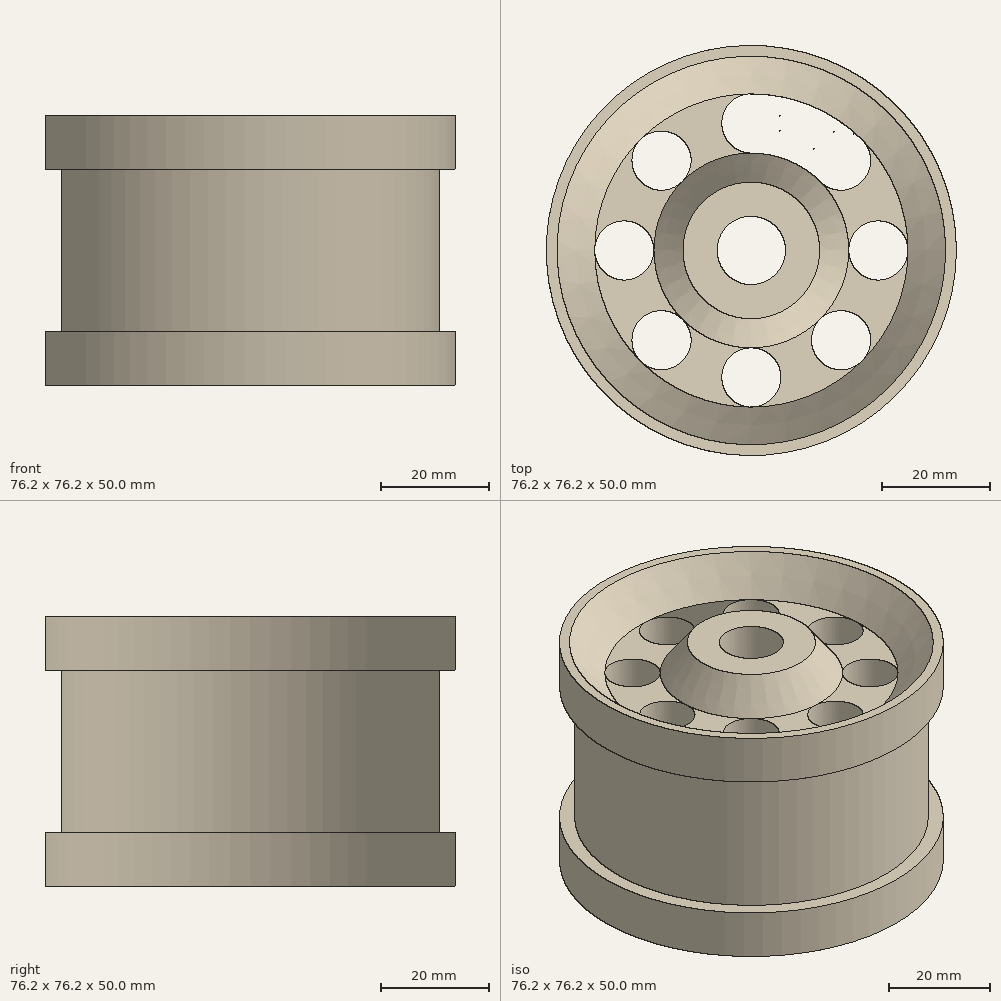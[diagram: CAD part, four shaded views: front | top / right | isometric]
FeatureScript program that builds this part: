
annotation { "Feature Type Name" : "Feature", "Feature Type Description" : "" }
export const myFeature = defineFeature(function(context is Context, id is Id, definition is map)
    precondition{}
    {
        {
            var Q0;
            Q0=qCreatedBy(makeId("Front.planeOp"),FACE);
            var sketch = newSketch(context, id + "F0", { "sketchPlane" : qUnion([Q0])});
            skLineSegment(sketch, "E0", {"start": v(-38.1, 40) * mm, "end": v(-38.1, 50) * mm});
            skLineSegment(sketch, "E1", {"start": v(-38.1, 50) * mm, "end": v(-36.1, 50) * mm});
            skLineSegment(sketch, "E2", {"start": v(-38.1, 40) * mm, "end": v(-35.1, 40) * mm});
            skLineSegment(sketch, "E3", {"start": v(-35.1, 10) * mm, "end": v(-35.1, 40) * mm});
            skLineSegment(sketch, "E4", {"start": v(-35.1, 0) * mm, "end": v(-29.1, 0) * mm});
            skLineSegment(sketch, "E5", {"start": v(-29.1, 0) * mm, "end": v(-29.1, 30) * mm});
            skLineSegment(sketch, "E6", {"start": v(-29.1, 30) * mm, "end": v(0, 30) * mm});
            skLineSegment(sketch, "E7", {"start": v(-29.1, 43) * mm, "end": v(-18.1, 43) * mm});
            skLineSegment(sketch, "E8", {"start": v(-18.1, 43) * mm, "end": v(-12.7, 50) * mm});
            skLineSegment(sketch, "E9", {"start": v(-12.7, 50) * mm, "end": v(0, 50) * mm});
            skLineSegment(sketch, "E10", {"start": v(-36.1, 50) * mm, "end": v(-29.1, 43) * mm});
            skLineSegment(sketch, "E11", {"start": v(-35.1, 10) * mm, "end": v(-38.1, 10) * mm});
            skLineSegment(sketch, "E12", {"start": v(-38.1, 10) * mm, "end": v(-38.1, 0) * mm});
            skLineSegment(sketch, "E13", {"start": v(-38.1, 0) * mm, "end": v(-35.1, 0) * mm});
            skLineSegment(sketch, "E14", {"start": v(0, 50) * mm, "end": v(0, 30) * mm});
            skSolve(sketch);
        }
        {
            var Q0;
            Q0=makeQuery(id+"F0.imprint","IMPRINT",FACE,{"disambiguationData":[TD([[makeQuery(id+"F0.imprint","IMPRINT",EDGE,{"derivedFrom":sQuery(id+"F0.wireOp",EDGE,"E0")}),-1.0]])]});
            var Q1;
            Q1=sQuery(id+"F0.wireOp",EDGE,"E14");
            revolve(context, id + "F1", {"entities" : qUnion([Q0]), "axis" : qUnion([Q1]), "revolveType" : RevolveType.FULL});
        }
        {
            var Q0;
            Q0=makeQuery(id+"F1.opRevolve","SWEPT_FACE",FACE,{"disambiguationData":[OSD([sQuery(id+"F0.wireOp",EDGE,"E7")])]});
            var sketch = newSketch(context, id + "F2", { "sketchPlane" : qUnion([Q0])});
            skCircle(sketch, "E15", {"center": v(-23.6, 0) * mm, "radius": 5.5 * mm});
            skCircle(sketch, "E16.1.0", {"center": v(-16.69, -16.69) * mm, "radius": 5.5 * mm});
            skCircle(sketch, "E16.2.0", {"center": v(0, -23.6) * mm, "radius": 5.5 * mm});
            skCircle(sketch, "E16.3.0", {"center": v(16.69, -16.69) * mm, "radius": 5.5 * mm});
            skCircle(sketch, "E16.4.0", {"center": v(23.6, 0) * mm, "radius": 5.5 * mm});
            skCircle(sketch, "E16.5.0", {"center": v(16.69, 16.69) * mm, "radius": 5.5 * mm});
            skCircle(sketch, "E16.6.0", {"center": v(0, 23.6) * mm, "radius": 5.5 * mm});
            skCircle(sketch, "E16.7.0", {"center": v(-16.69, 16.69) * mm, "radius": 5.5 * mm});
            skPoint(sketch, "E16.center", {"position": v(0, 0) * mm});
            skSolve(sketch);
        }
        {
            var Q0;
            Q0 = qSketchRegion(id + "F2", true);
            extrude(context, id + "F3", {"entities" : qUnion([Q0]), "operationType" : NewBodyOperationType.REMOVE, "oppositeDirection" : true, "depth" : 25 * mm, "offsetDistance" : 25 * mm});
        }
        {
            var Q0;
            Q0=makeQuery(id+"F1.opRevolve","SWEPT_FACE",FACE,{"disambiguationData":[OSD([sQuery(id+"F0.wireOp",EDGE,"E9")])]});
            var sketch = newSketch(context, id + "F4", { "sketchPlane" : qUnion([Q0])});
            skCircle(sketch, "E17", {"center": v(0, 0) * mm, "radius": 6.35 * mm});
            skSolve(sketch);
        }
        {
            var Q0;
            Q0 = qSketchRegion(id + "F4", true);
            extrude(context, id + "F5", {"entities" : qUnion([Q0]), "operationType" : NewBodyOperationType.REMOVE, "oppositeDirection" : true, "depth" : 25 * mm, "offsetDistance" : 25 * mm});
        }
    });
